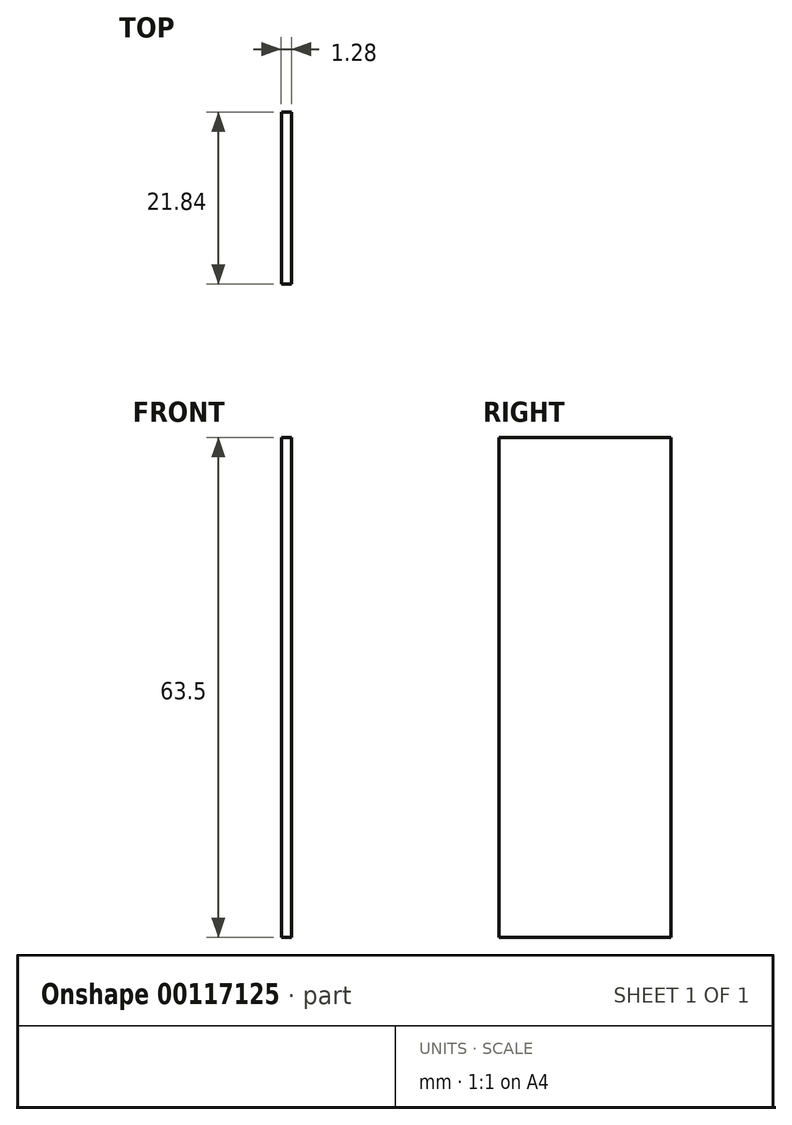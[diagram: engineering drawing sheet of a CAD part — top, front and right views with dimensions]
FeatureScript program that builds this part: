
annotation { "Feature Type Name" : "Feature", "Feature Type Description" : "" }
export const myFeature = defineFeature(function(context is Context, id is Id, definition is map)
    precondition{}
    {
        {
            var Q0;
            Q0=qCreatedBy(makeId("Front.planeOp"),FACE);
            var sketch = newSketch(context, id + "F0", { "sketchPlane" : qUnion([Q0])});
            skLineSegment(sketch, "E0.bottom", {"start": v(-0.63, -31.75) * mm, "end": v(0.64, -31.75) * mm});
            skLineSegment(sketch, "E0.top", {"start": v(-0.64, 31.75) * mm, "end": v(0.63, 31.75) * mm});
            skLineSegment(sketch, "E0.left", {"start": v(-0.63, -31.75) * mm, "end": v(-0.64, 31.75) * mm});
            skLineSegment(sketch, "E0.right", {"start": v(0.64, -31.75) * mm, "end": v(0.63, 31.75) * mm});
            skPoint(sketch, "E0.middle", {"position": v(0, 0) * mm});
            skSolve(sketch);
        }
        {
            var Q0;
            Q0 = qSketchRegion(id + "F0", true);
            extrude(context, id + "F1", {"entities" : qUnion([Q0]), "oppositeDirection" : true, "depth" : 21.84 * mm});
        }
    });
